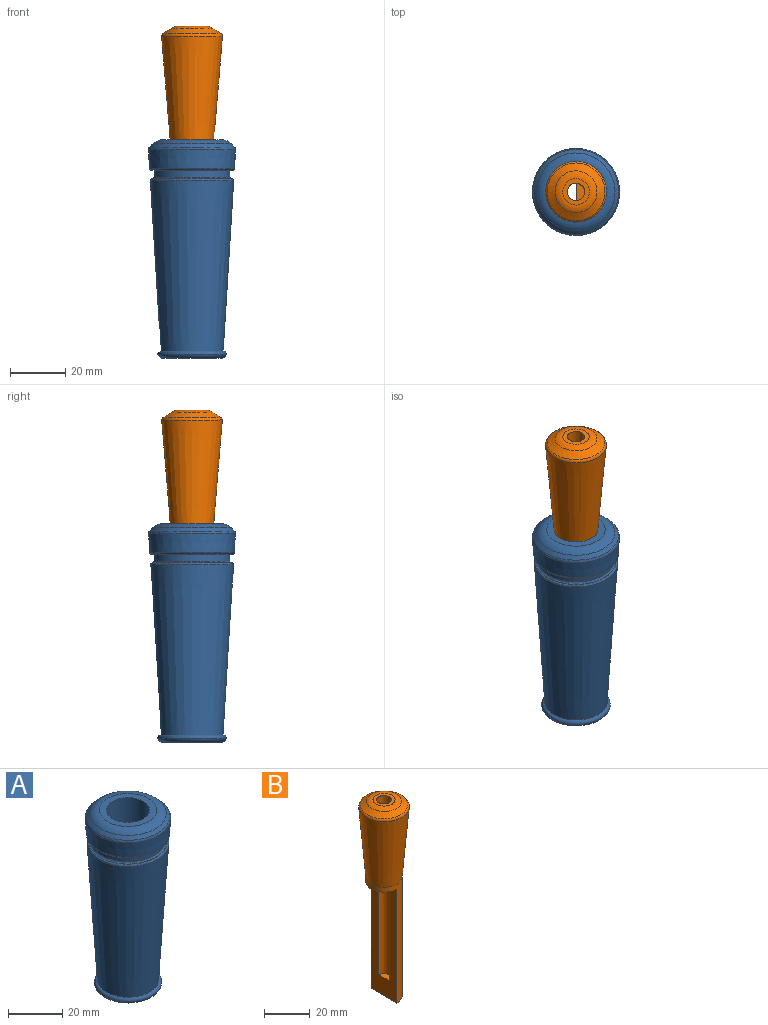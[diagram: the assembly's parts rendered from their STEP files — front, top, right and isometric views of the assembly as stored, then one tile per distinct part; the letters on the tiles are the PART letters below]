
ASSEMBLY  parts=2 mates=1
PART A: 17 faces, bbox 34.3x34.3x79.4 mm
  f0: plane 21.19x21.19mm, normal (0,0,1), area 154.8mm2, adj f8,f9
  f1: cone r=12.7mm half-angle=45deg, axis (0,0,-1), area 169mm2, adj f9,f10
  f2: cone r=15.88mm half-angle=3.5deg, axis (0,0,1), area 666.2mm2, adj f10,f11
  f3: plane 29.58x29.58mm, normal (0,0,-1), area 88.9mm2, adj f4,f11
  f4: cylinder r=13.8mm len=27.6mm, axis (0,0,1), area 220.2mm2, adj f3,f13
  f5: plane 29.03x29.03mm, normal (0,0,1), area 7.4mm2, adj f12,f13
  f6: cone r=15.19mm half-angle=3.5deg, axis (0,0,1), area 5157.1mm2, adj f12,f14
  f7: plane 21.88x21.88mm, normal (0,0,-1), area 152mm2, adj f15,f16
  f8: cylinder r=7.94mm len=78.87mm, axis (0,0,1), area 3933.3mm2, adj f0,f16
  f9: torus R=10.6mm, axis (0,0,1), area 313.1mm2, adj f0,f1
  f10: torus R=14.57mm, axis (0,0,-1), area 106.3mm2, adj f1,f2
  f11: torus R=14.79mm, axis (0,0,-1), area 91.4mm2, adj f2,f3
  f12: torus R=14.51mm, axis (0,0,-1), area 97.2mm2, adj f5,f6
  f13: torus R=14.43mm, axis (0,0,-1), area 87.9mm2, adj f4,f5
  f14: torus R=11.18mm, axis (0,0,1), area 139.1mm2, adj f6,f15
  f15: torus R=10.94mm, axis (0,0,-1), area 160mm2, adj f7,f14
  f16: torus R=8.45mm, axis (0,0,1), area 40.7mm2, adj f7,f8
PART B: 11 faces, bbox 23.9x23.9x104.8 mm
  f0: plane 15.88x7.94mm, normal (0,0,-1), area 99mm2, adj f2,f5
  f1: cone r=7.94mm half-angle=4.8deg, axis (0,0,1), area 2235.9mm2, adj f2,f10
  f2: cylinder r=7.94mm len=63.5mm, axis (0,0,-1), area 1646.8mm2, adj f0,f1,f5,f6
  f3: plane 9.62x9.62mm, normal (0,0,1), area 41.1mm2, adj f7,f9
  f4: cone r=11.11mm half-angle=56.3deg, axis (0,0,-1), area 195.6mm2, adj f9,f10
  f5: plane 60.96x15.88mm, normal (-1,0,0), area 641.1mm2, adj f0,f2,f6,f7,f8
  f6: plane 15.88x7.94mm, normal (0,0,-1), area 83.1mm2, adj f2,f5,f7
  f7: cylinder r=3.17mm len=95.25mm, axis (0,0,1), area 1387.1mm2, adj f3,f5,f6,f8
  f8: plane 6.35x3.18mm, normal (0,0,1), area 15.8mm2, adj f5,f7
  f9: torus R=4.81mm, axis (0,0,-1), area 117.5mm2, adj f3,f4
  f10: torus R=9.78mm, axis (0,0,1), area 92.5mm2, adj f1,f4
PLACE A at identity
PLACE B t=(-43.14,0,0)mm
MATE revolute B.f1 <-> A.f8  axis (0,0,-1) through (-29.29,0,0)mm
